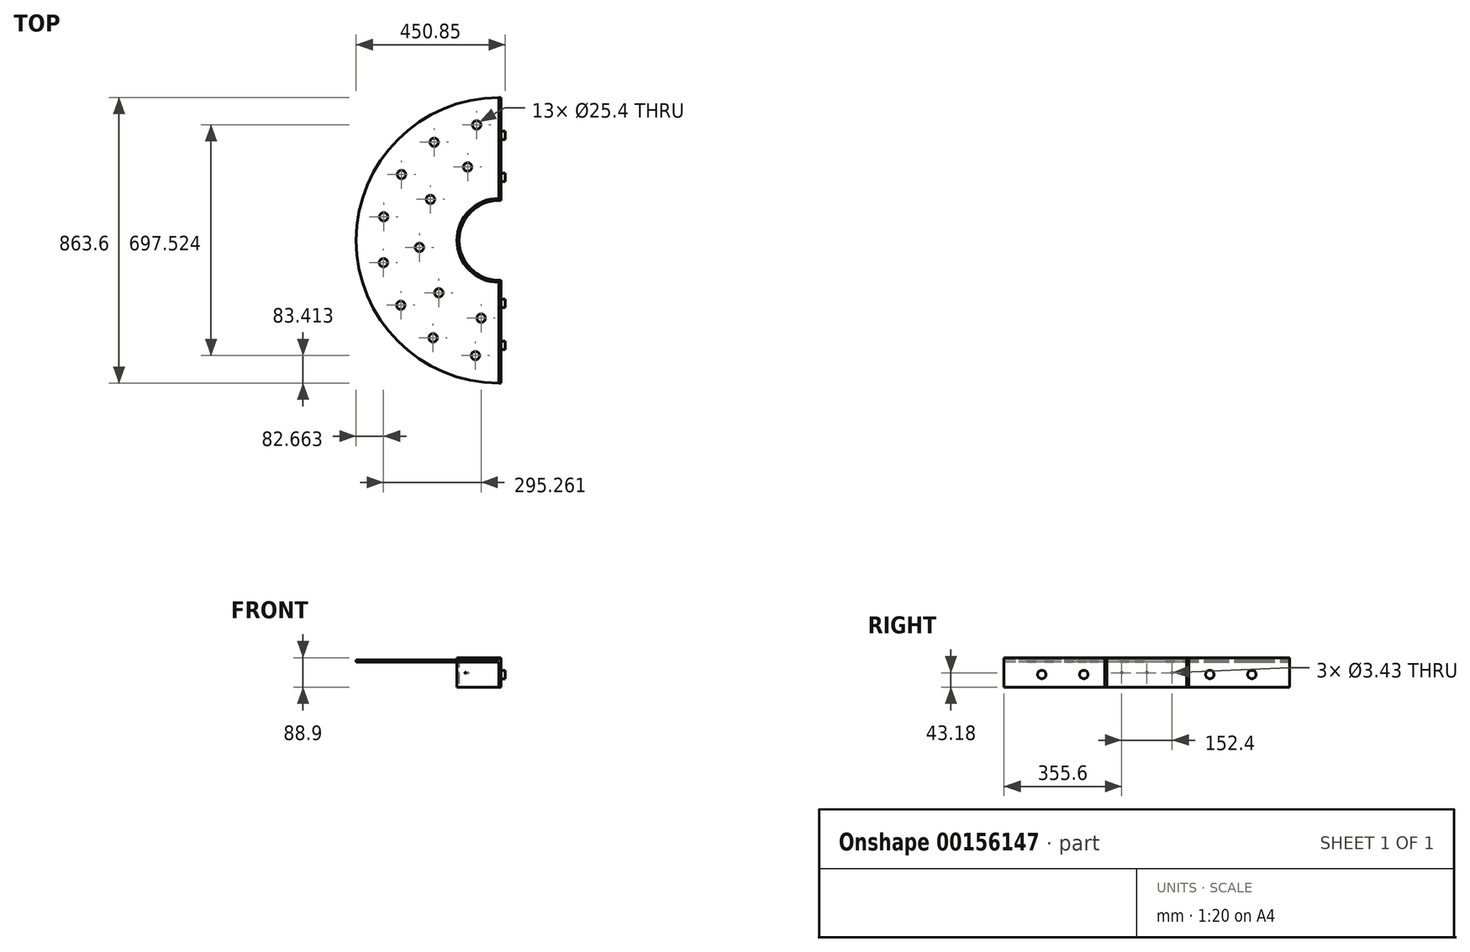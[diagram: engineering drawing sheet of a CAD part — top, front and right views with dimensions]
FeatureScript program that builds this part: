
annotation { "Feature Type Name" : "Feature", "Feature Type Description" : "" }
export const myFeature = defineFeature(function(context is Context, id is Id, definition is map)
    precondition{}
    {
        {
            var Q0;
            Q0=qCreatedBy(makeId("Top.planeOp"),FACE);
            var sketch = newSketch(context, id + "F0", { "sketchPlane" : qUnion([Q0])});
            skCircle(sketch, "E0", {"center": v(0, 0) * mm, "radius": 127 * mm});
            skCircle(sketch, "E1", {"center": v(0, 0) * mm, "radius": 431.8 * mm});
            skSolve(sketch);
        }
        {
            var Q0;
            Q0=makeQuery(id+"F0.imprint","IMPRINT",FACE,{"disambiguationData":[TD([[makeQuery(id+"F0.imprint","IMPRINT",EDGE,{"derivedFrom":sQuery(id+"F0.wireOp",EDGE,"E0")}),-1.0]])]});
            extrude(context, id + "F1", {"entities" : qUnion([Q0]), "depth" : 6.35 * mm});
        }
        {
            var Q0;
            Q0=makeQuery(id+"F1.opExtrude","CAP_FACE",FACE,{"disambiguationData":[OSD([sQuery(id+"F0.wireOp",EDGE,"E0"),sQuery(id+"F0.wireOp",EDGE,"E1")])],"isStart":false});
            var sketch = newSketch(context, id + "F2", { "sketchPlane" : qUnion([Q0])});
            skLineSegment(sketch, "E2", {"start": v(0, 127) * mm, "end": v(0, 431.8) * mm});
            skLineSegment(sketch, "E3", {"start": v(0, -127) * mm, "end": v(0, -431.8) * mm});
            skArc(sketch, "E4", {"start": v(0, -127) * mm, "mid": v(126.7, 0) * mm, "end": v(0, 127) * mm});
            skArc(sketch, "E5", {"start": v(0, -431.8) * mm, "mid": v(431.8, 0) * mm, "end": v(0, 431.8) * mm});
            skSolve(sketch);
        }
        {
            var Q0;
            {var subQ0=sQuery(id+"F2.wireOp",EDGE,"E2");Q0=makeQuery(id+"F2.imprint","IMPRINT",FACE,{"disambiguationData":[TD([[makeQuery(id+"F2.imprint","IMPRINT",EDGE,{"derivedFrom":subQ0}),-1.0]])]});}
            extrude(context, id + "F3", {"entities" : qUnion([Q0]), "operationType" : NewBodyOperationType.REMOVE, "oppositeDirection" : true, "depth" : 25.4 * mm});
        }
        {
            var Q0;
            Q0=makeQuery(id+"F3.boolean.opBoolean","COPY",FACE,{"derivedFrom":makeQuery(id+"F3.opExtrude","SWEPT_FACE",FACE,{"disambiguationData":[OSD([sQuery(id+"F2.wireOp",EDGE,"E3")])]})});
            var sketch = newSketch(context, id + "F4", { "sketchPlane" : qUnion([Q0])});
            skLineSegment(sketch, "E6.bottom", {"start": v(-431.8, 12.7) * mm, "end": v(-127, 12.7) * mm});
            skLineSegment(sketch, "E6.top", {"start": v(-431.8, -76.2) * mm, "end": v(-127, -76.2) * mm});
            skLineSegment(sketch, "E6.left", {"start": v(-431.8, 12.7) * mm, "end": v(-431.8, -76.2) * mm});
            skLineSegment(sketch, "E6.right", {"start": v(-127, 12.7) * mm, "end": v(-127, -76.2) * mm});
            skSolve(sketch);
        }
        {
            var Q0;
            Q0 = qSketchRegion(id + "F4", true);
            extrude(context, id + "F5", {"entities" : qUnion([Q0]), "operationType" : NewBodyOperationType.ADD, "depth" : 6.35 * mm});
        }
        {
            var Q0;
            Q0=makeQuery(id+"F5.opExtrude","CAP_FACE",FACE,{"disambiguationData":[OSD([sQuery(id+"F4.wireOp",EDGE,"E6.bottom"),sQuery(id+"F4.wireOp",EDGE,"E6.top"),sQuery(id+"F4.wireOp",EDGE,"E6.left"),sQuery(id+"F4.wireOp",EDGE,"E6.right")])],"isStart":false});
            var sketch = newSketch(context, id + "F6", { "sketchPlane" : qUnion([Q0])});
            skSolve(sketch);
        }
        {
            var Q0;
            Q0=makeQuery(id+"F3.boolean.opBoolean","COPY",FACE,{"derivedFrom":makeQuery(id+"F3.opExtrude","SWEPT_FACE",FACE,{"disambiguationData":[OSD([sQuery(id+"F2.wireOp",EDGE,"E2")])]})});
            var sketch = newSketch(context, id + "F7", { "sketchPlane" : qUnion([Q0])});
            skLineSegment(sketch, "E7.bottom", {"start": v(127, 12.7) * mm, "end": v(431.8, 12.7) * mm});
            skLineSegment(sketch, "E7.top", {"start": v(127, -76.2) * mm, "end": v(431.8, -76.2) * mm});
            skLineSegment(sketch, "E7.left", {"start": v(127, 12.7) * mm, "end": v(127, -76.2) * mm});
            skLineSegment(sketch, "E7.right", {"start": v(431.8, 12.7) * mm, "end": v(431.8, -76.2) * mm});
            skSolve(sketch);
        }
        {
            var Q0;
            Q0 = qSketchRegion(id + "F7", true);
            extrude(context, id + "F8", {"entities" : qUnion([Q0]), "operationType" : NewBodyOperationType.ADD, "depth" : 6.35 * mm});
        }
        {
            var Q0;
            Q0=makeQuery(id+"F1.opExtrude","CAP_FACE",FACE,{"disambiguationData":[OSD([sQuery(id+"F0.wireOp",EDGE,"E0"),sQuery(id+"F0.wireOp",EDGE,"E1")])],"isStart":false});
            var sketch = newSketch(context, id + "F9", { "sketchPlane" : qUnion([Q0])});
            skArc(sketch, "E8", {"start": v(0, 127) * mm, "mid": v(-127, 0) * mm, "end": v(0, -127) * mm});
            skArc(sketch, "E9.0", {"start": v(0, 120.65) * mm, "mid": v(-120.65, 0) * mm, "end": v(0, -120.65) * mm});
            skLineSegment(sketch, "E10", {"start": v(0, 127) * mm, "end": v(6.35, 127) * mm});
            skLineSegment(sketch, "E11", {"start": v(6.35, 127) * mm, "end": v(6.35, 120.65) * mm});
            skLineSegment(sketch, "E12", {"start": v(6.35, 120.65) * mm, "end": v(0, 120.65) * mm});
            skLineSegment(sketch, "E13", {"start": v(0, -120.65) * mm, "end": v(6.35, -120.65) * mm});
            skLineSegment(sketch, "E14", {"start": v(6.35, -120.65) * mm, "end": v(6.35, -127) * mm});
            skLineSegment(sketch, "E15", {"start": v(6.35, -127) * mm, "end": v(0, -127) * mm});
            skSolve(sketch);
        }
        {
            var Q0;
            Q0 = qSketchRegion(id + "F9", true);
            extrude(context, id + "F10", {"entities" : qUnion([Q0]), "depth" : 6.35 * mm, "hasSecondDirection" : true, "secondDirectionOppositeDirection" : true, "secondDirectionDepth" : 82.55 * mm});
        }
        {
            var Q0;
            Q0=makeQuery(id+"F6.imprint","IMPRINT",FACE,{"disambiguationData":[TD([[makeQuery(id+"F6.imprint","IMPRINT",EDGE,{"derivedFrom":makeQuery(id+"F5.opExtrude","CAP_EDGE",EDGE,{"disambiguationData":[OSD([sQuery(id+"F4.wireOp",EDGE,"E6.bottom")])],"isStart":false})}),-1.0]])]});
            var sketch = newSketch(context, id + "F11", { "sketchPlane" : qUnion([Q0])});
            skArc(sketch, "E16", {"start": v(-177.8, -38.1) * mm, "mid": v(-190.5, -25.4) * mm, "end": v(-203.2, -38.1) * mm});
            skArc(sketch, "E17", {"start": v(-304.8, -38.1) * mm, "mid": v(-317.5, -25.4) * mm, "end": v(-330.2, -38.1) * mm});
            skArc(sketch, "E18.MirrorCS", {"start": v(177.8, -38.1) * mm, "mid": v(190.5, -25.4) * mm, "end": v(203.2, -38.1) * mm});
            skArc(sketch, "E19.MirrorCS", {"start": v(304.8, -38.1) * mm, "mid": v(317.5, -25.4) * mm, "end": v(330.2, -38.1) * mm});
            skArc(sketch, "E20", {"start": v(-330.2, -38.1) * mm, "mid": v(-317.5, -50.8) * mm, "end": v(-304.8, -38.1) * mm});
            skArc(sketch, "E21", {"start": v(-203.2, -38.1) * mm, "mid": v(-190.5, -50.8) * mm, "end": v(-177.8, -38.1) * mm});
            skArc(sketch, "E22", {"start": v(177.8, -38.1) * mm, "mid": v(190.5, -50.8) * mm, "end": v(203.2, -38.1) * mm});
            skArc(sketch, "E23", {"start": v(304.8, -38.1) * mm, "mid": v(317.5, -50.8) * mm, "end": v(330.2, -38.1) * mm});
            skSolve(sketch);
        }
        {
            var Q0;
            Q0 = qSketchRegion(id + "F11", true);
            extrude(context, id + "F12", {"entities" : qUnion([Q0]), "operationType" : NewBodyOperationType.ADD, "depth" : 12.7 * mm});
        }
        {
            var Q0;
            Q0=qCreatedBy(makeId("Right.planeOp"),FACE);
            var sketch = newSketch(context, id + "F13", { "sketchPlane" : qUnion([Q0])});
            skLineSegment(sketch, "E24", {"start": v(128.64, -33.02) * mm, "end": v(-125.47, -33.02) * mm});
            skLineSegment(sketch, "E25", {"start": v(76.2, 0) * mm, "end": v(76.2, -77.85) * mm});
            skLineSegment(sketch, "E26", {"start": v(-76.2, 0) * mm, "end": v(-76.2, -74.27) * mm});
            skCircle(sketch, "E27", {"center": v(76.2, -33.02) * mm, "radius": 1.71 * mm});
            skCircle(sketch, "E28", {"center": v(-76.2, -33.02) * mm, "radius": 1.71 * mm});
            skCircle(sketch, "E29", {"center": v(0, -33.02) * mm, "radius": 1.71 * mm});
            skSolve(sketch);
        }
        {
            var Q0;
            Q0 = qSketchRegion(id + "F13", true);
            extrude(context, id + "F14", {"entities" : qUnion([Q0]), "operationType" : NewBodyOperationType.REMOVE, "endBound" : BoundingType.THROUGH_ALL, "oppositeDirection" : true, "depth" : 25.4 * mm});
        }
        {
            var Q0;
            Q0=makeQuery(id+"F1.opExtrude","CAP_FACE",FACE,{"disambiguationData":[OSD([sQuery(id+"F0.wireOp",EDGE,"E0"),sQuery(id+"F0.wireOp",EDGE,"E1")])],"isStart":false});
            var sketch = newSketch(context, id + "F15", { "sketchPlane" : qUnion([Q0])});
            skArc(sketch, "E30.0", {"start": v(0, 355.6) * mm, "mid": v(-355.6, 0) * mm, "end": v(0, -355.6) * mm});
            skCircle(sketch, "E31", {"center": v(-67.49, 349.14) * mm, "radius": 12.7 * mm});
            skCircle(sketch, "E32.1.0", {"center": v(-195.96, 296.73) * mm, "radius": 12.7 * mm});
            skCircle(sketch, "E32.2.0", {"center": v(-294.6, 199.16) * mm, "radius": 12.7 * mm});
            skCircle(sketch, "E32.3.0", {"center": v(-348.39, 71.26) * mm, "radius": 12.7 * mm});
            skCircle(sketch, "E32.4.0", {"center": v(-349.14, -67.49) * mm, "radius": 12.7 * mm});
            skCircle(sketch, "E32.5.0", {"center": v(-296.73, -195.96) * mm, "radius": 12.7 * mm});
            skCircle(sketch, "E32.6.0", {"center": v(-199.16, -294.6) * mm, "radius": 12.7 * mm});
            skCircle(sketch, "E32.7.0", {"center": v(-71.26, -348.39) * mm, "radius": 12.7 * mm});
            skCircle(sketch, "E32.8.0", {"center": v(67.49, -349.14) * mm, "radius": 12.7 * mm});
            skCircle(sketch, "E32.9.0", {"center": v(195.96, -296.73) * mm, "radius": 12.7 * mm});
            skCircle(sketch, "E32.10.0", {"center": v(294.6, -199.16) * mm, "radius": 12.7 * mm});
            skCircle(sketch, "E32.11.0", {"center": v(348.39, -71.26) * mm, "radius": 12.7 * mm});
            skCircle(sketch, "E32.12.0", {"center": v(349.14, 67.49) * mm, "radius": 12.7 * mm});
            skCircle(sketch, "E32.13.0", {"center": v(296.73, 195.96) * mm, "radius": 12.7 * mm});
            skCircle(sketch, "E32.14.0", {"center": v(199.16, 294.6) * mm, "radius": 12.7 * mm});
            skCircle(sketch, "E33.1.15.0", {"center": v(71.26, 348.39) * mm, "radius": 12.7 * mm});
            skArc(sketch, "E34.0", {"start": v(0, 241.3) * mm, "mid": v(-241.3, 0) * mm, "end": v(0, -241.3) * mm});
            skCircle(sketch, "E35", {"center": v(-94.67, 221.96) * mm, "radius": 12.7 * mm});
            skCircle(sketch, "E36.1.0", {"center": v(-207.05, 123.92) * mm, "radius": 12.7 * mm});
            skCircle(sketch, "E36.2.0", {"center": v(-240.35, -21.44) * mm, "radius": 12.7 * mm});
            skCircle(sketch, "E36.3.0", {"center": v(-181.84, -158.62) * mm, "radius": 12.7 * mm});
            skCircle(sketch, "E36.4.0", {"center": v(-53.88, -235.2) * mm, "radius": 12.7 * mm});
            skCircle(sketch, "E36.5.0", {"center": v(94.67, -221.96) * mm, "radius": 12.7 * mm});
            skCircle(sketch, "E36.6.0", {"center": v(207.05, -123.92) * mm, "radius": 12.7 * mm});
            skCircle(sketch, "E36.7.0", {"center": v(240.35, 21.44) * mm, "radius": 12.7 * mm});
            skCircle(sketch, "E36.8.0", {"center": v(181.84, 158.62) * mm, "radius": 12.7 * mm});
            skCircle(sketch, "E36.9.0", {"center": v(53.88, 235.2) * mm, "radius": 12.7 * mm});
            skSolve(sketch);
        }
        {
            var Q0;
            Q0 = qSketchRegion(id + "F15", true);
            extrude(context, id + "F16", {"entities" : qUnion([Q0]), "operationType" : NewBodyOperationType.REMOVE, "endBound" : BoundingType.THROUGH_ALL, "oppositeDirection" : true, "depth" : 25.4 * mm});
        }
    });
